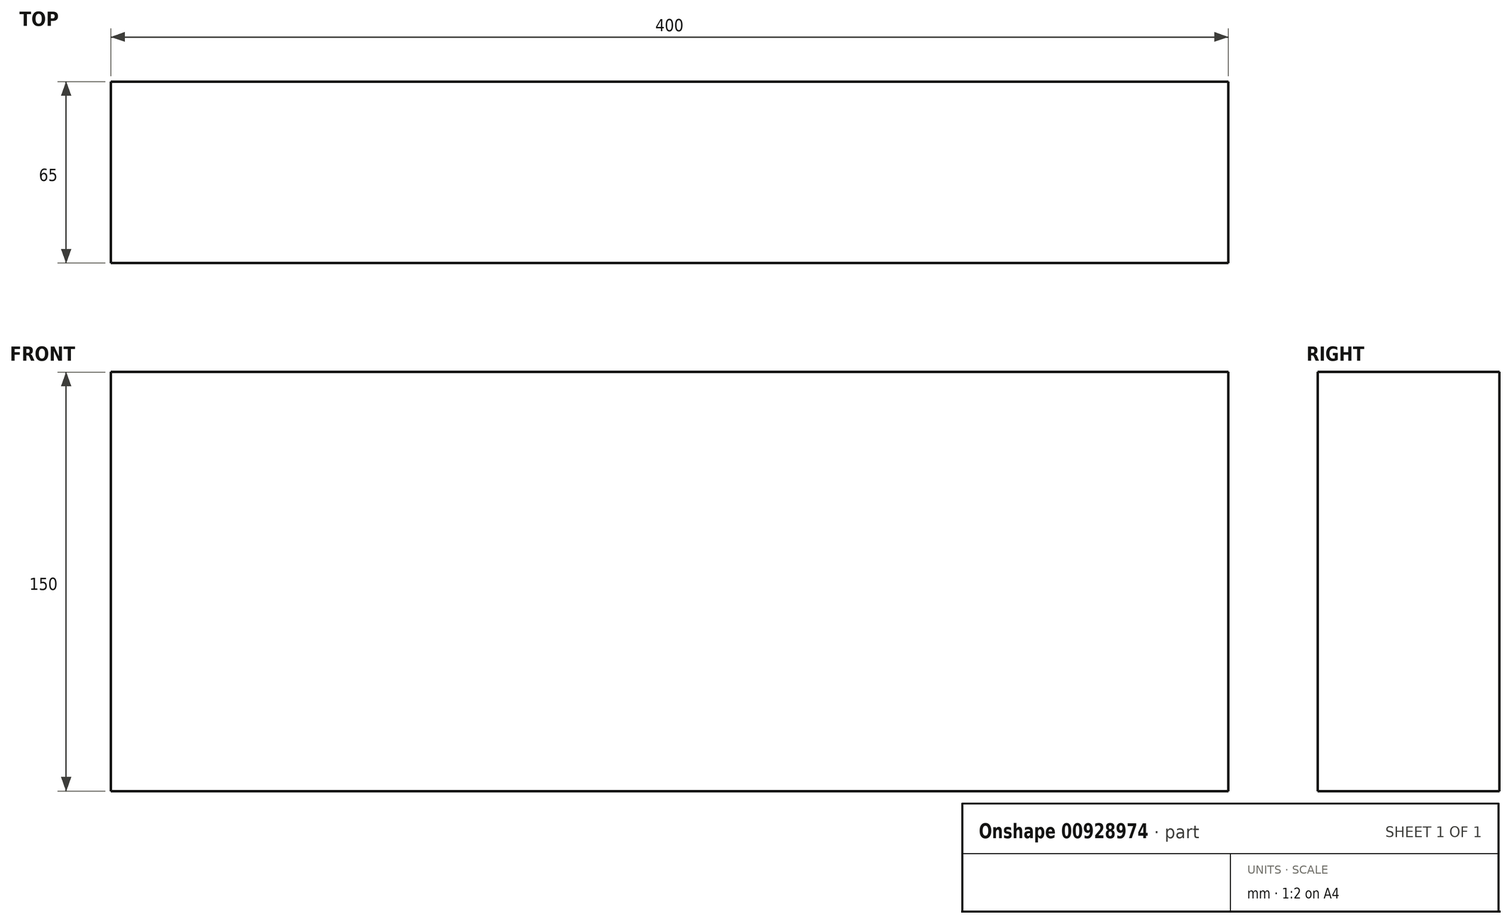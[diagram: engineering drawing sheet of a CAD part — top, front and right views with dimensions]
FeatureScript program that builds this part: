
annotation { "Feature Type Name" : "Feature", "Feature Type Description" : "" }
export const myFeature = defineFeature(function(context is Context, id is Id, definition is map)
    precondition{}
    {
        {
            var Q0;
            Q0=qCreatedBy(makeId("Front.planeOp"),FACE);
            var sketch = newSketch(context, id + "F0", { "sketchPlane" : qUnion([Q0])});
            skLineSegment(sketch, "E0.bottom", {"start": v(-27.81, 136.1) * mm, "end": v(372.19, 136.1) * mm});
            skLineSegment(sketch, "E0.top", {"start": v(-27.81, -13.9) * mm, "end": v(372.19, -13.9) * mm});
            skLineSegment(sketch, "E0.left", {"start": v(-27.81, 136.1) * mm, "end": v(-27.81, -13.9) * mm});
            skLineSegment(sketch, "E0.right", {"start": v(372.19, 136.1) * mm, "end": v(372.19, -13.9) * mm});
            skSolve(sketch);
        }
        {
            var Q0;
            Q0=makeQuery(id+"F0.imprint","IMPRINT",FACE,{"disambiguationData":[TD([[makeQuery(id+"F0.imprint","IMPRINT",EDGE,{"derivedFrom":sQuery(id+"F0.wireOp",EDGE,"E0.bottom")}),-1.0]])]});
            extrude(context, id + "F1", {"entities" : qUnion([Q0]), "depth" : 65 * mm, "offsetDistance" : 25 * mm});
        }
    });
